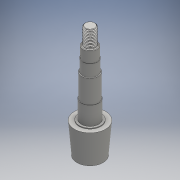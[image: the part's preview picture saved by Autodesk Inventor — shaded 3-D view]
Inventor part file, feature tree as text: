
AUTODESK INVENTOR PART (.ipt)
format: ipt  version: 2016 (Build 200138000, 138)  size: 334,336 bytes
history: native  units: mm
features: sketch x10, extrude x7, loft x1, chamfer x1, fillet x1, helix x1, other x1
ambient origin geometry x8: Origin, YZ Plane, XZ Plane, XY Plane, X Axis, Y Axis, Z Axis, Center Point
bodies: Solid1 (feature_tree)
feature tree (22):
  extrude  "Extrusion1"  Depth=35.8mm TaperAngle=0.0deg
  loft  "Loft1"
  extrude  "Extrusion2"  Depth=25.6mm
  extrude  "Extrusion3"  Depth=20.66mm
  extrude  "Extrusion4"  Depth=19.68mm
  extrude  "Extrusion5"  Depth=17.64mm
  extrude  "Extrusion6"  Depth=16.62mm
  extrude  "Extrusion7"  Depth=12.66mm
  chamfer  "Chamfer1"  Distance=20.4mm
  fillet  "Fillet1"  Radius=1.0mm
  sketch  "Sketch9"  dims[d27=1.0mm d28=2.0mm d29=45.0deg d30=1.0mm d31=1.5mm]
  helix  "Coil1"  [1 undecoded]
  sketch  "Sketch1"  dims[d1=31.0mm d2=35.8mm d3=0.0mm]
  sketch  "Sketch2"  dims[d4=36.7mm d5=0.0mm d6=90.0deg]
  other  "Edges1"
  sketch  "Sketch3"  dims[d7=0.0mm d8=90.0deg d9=25.6mm]
  sketch  "Sketch4"  dims[d10=1.0mm d11=0.0mm d12=20.66mm]
  sketch  "Sketch5"  dims[d13=21.7mm d14=0.0mm d15=19.68mm]
  sketch  "Sketch6"  dims[d16=27.3mm d17=0.0mm d18=17.64mm]
  sketch  "Sketch7"  dims[d19=14.2mm d20=0.0mm d21=16.62mm]
  sketch  "Sketch8"  dims[d22=12.8mm d23=0.0mm d24=12.66mm d25=20.4mm d26=0.0mm]
  sketch  "Sketch10"  dims[d33=2.0mm d34=0.2mm d35=1.5mm d36=22.0mm d37=10.0mm d38=0.0mm d39=90.0deg d40=90.0deg d41=0.0mm d42=0.0mm]
note: 1 required parameter value undecoded (feature->parameter linkage not recoverable at this tier; creation-order binding heuristic only, values carry confidence <= 0.55)
